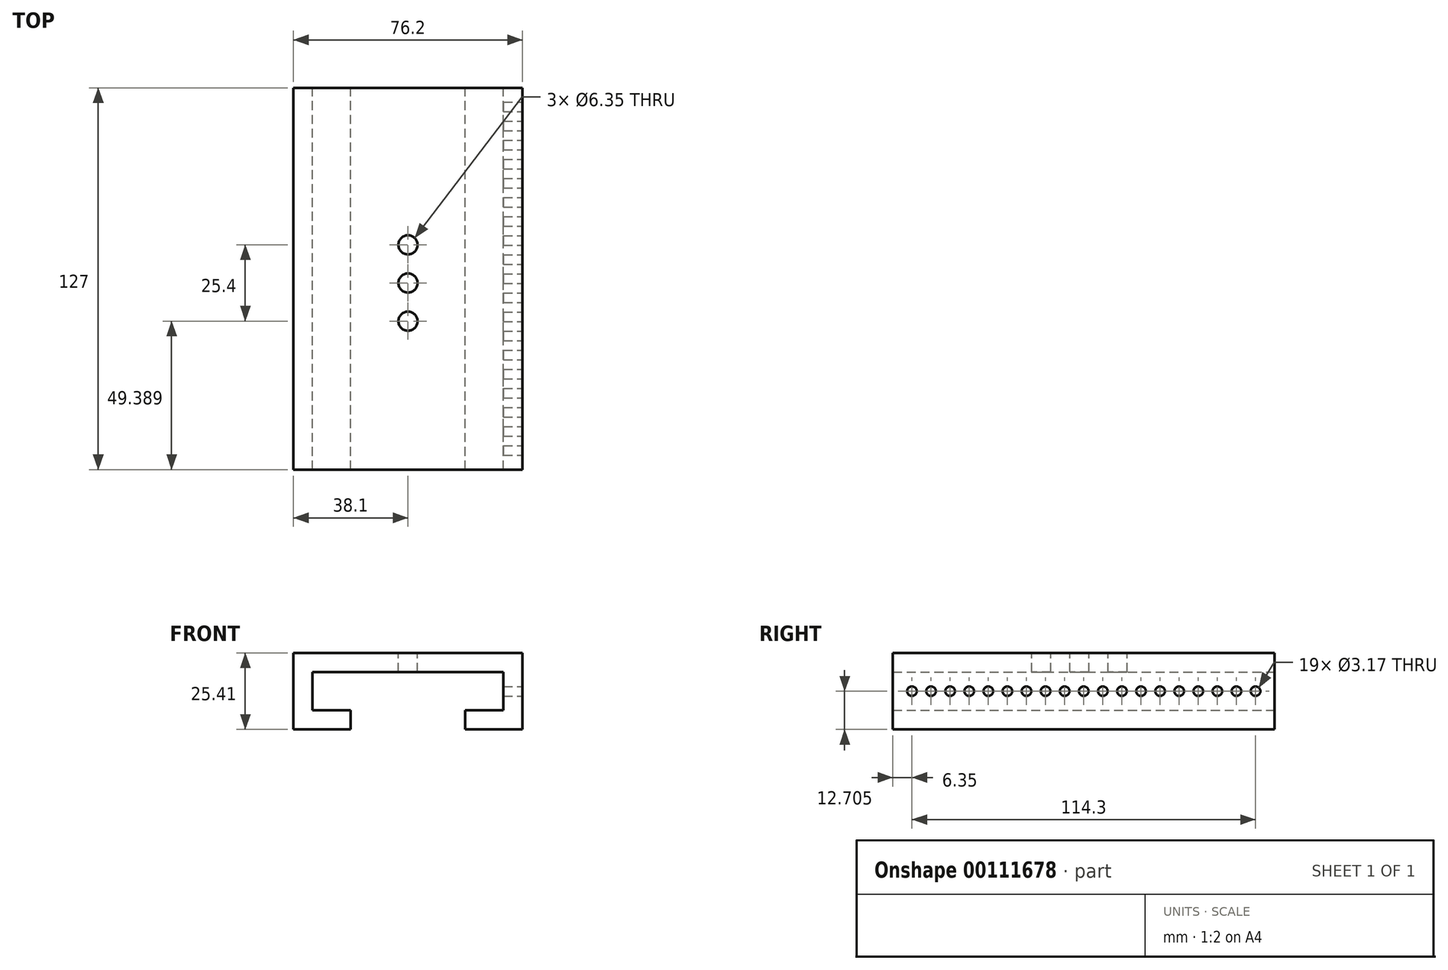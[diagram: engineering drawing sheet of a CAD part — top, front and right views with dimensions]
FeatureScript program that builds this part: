
annotation { "Feature Type Name" : "Feature", "Feature Type Description" : "" }
export const myFeature = defineFeature(function(context is Context, id is Id, definition is map)
    precondition{}
    {
        {
            var Q0;
            Q0=qCreatedBy(makeId("Front.planeOp"),FACE);
            var sketch = newSketch(context, id + "F0", { "sketchPlane" : qUnion([Q0])});
            skLineSegment(sketch, "E0.bottom", {"start": v(31.75, 3.17) * mm, "end": v(-31.75, 3.17) * mm});
            skLineSegment(sketch, "E0.top", {"start": v(31.75, -3.18) * mm, "end": v(-31.75, -3.18) * mm});
            skPoint(sketch, "E0.middle", {"position": v(0, 0) * mm});
            skLineSegment(sketch, "E1.bottom", {"start": v(31.75, 3.17) * mm, "end": v(38.1, 3.17) * mm});
            skLineSegment(sketch, "E2.bottom", {"start": v(-31.75, 3.17) * mm, "end": v(-38.1, 3.17) * mm});
            skLineSegment(sketch, "E3", {"start": v(-31.75, -3.18) * mm, "end": v(-31.75, -15.88) * mm});
            skLineSegment(sketch, "E4", {"start": v(-31.75, -15.88) * mm, "end": v(-19.05, -15.88) * mm});
            skLineSegment(sketch, "E5", {"start": v(-19.05, -15.88) * mm, "end": v(-19.05, -22.23) * mm});
            skLineSegment(sketch, "E6", {"start": v(-19.05, -22.23) * mm, "end": v(-38.1, -22.23) * mm});
            skLineSegment(sketch, "E7", {"start": v(-38.1, -22.23) * mm, "end": v(-38.1, 3.17) * mm});
            skLineSegment(sketch, "E8", {"start": v(31.75, -3.18) * mm, "end": v(31.75, -15.88) * mm});
            skLineSegment(sketch, "E9", {"start": v(31.75, -15.88) * mm, "end": v(19.05, -15.88) * mm});
            skLineSegment(sketch, "E10", {"start": v(19.05, -15.88) * mm, "end": v(19.05, -22.23) * mm});
            skLineSegment(sketch, "E11", {"start": v(19.05, -22.23) * mm, "end": v(38.1, -22.23) * mm});
            skLineSegment(sketch, "E12", {"start": v(38.1, -22.23) * mm, "end": v(38.1, 3.17) * mm});
            skSolve(sketch);
        }
        {
            var Q0;
            Q0=makeQuery(id+"F0.imprint","IMPRINT",FACE,{"disambiguationData":[TD([[makeQuery(id+"F0.imprint","IMPRINT",EDGE,{"derivedFrom":sQuery(id+"F0.wireOp",EDGE,"E0.bottom")}),1.0]])]});
            extrude(context, id + "F1", {"entities" : qUnion([Q0]), "endBound" : BoundingType.SYMMETRIC, "depth" : 127 * mm});
        }
        {
            var Q0;
            {var subQ0=sQuery(id+"F0.wireOp",EDGE,"E2.bottom");var subQ1=sQuery(id+"F0.wireOp",EDGE,"E1.bottom");var subQ2=sQuery(id+"F0.wireOp",EDGE,"E0.bottom");Q0=makeQuery(id+"FXCp8q9W37Aup2r_1.boolean.opBoolean","MERGE",FACE,{"derivedFrom":[makeQuery(id+"F1.opExtrude","SWEPT_FACE",FACE,{"disambiguationData":[OSD([subQ2,subQ1,subQ0])]}),makeQuery(id+"FXCp8q9W37Aup2r_1.opExtrude","SWEPT_FACE",FACE,{"disambiguationData":[OSD([subQ2,subQ1,subQ0])]})]});}
            var sketch = newSketch(context, id + "F2", { "sketchPlane" : qUnion([Q0])});
            skCircle(sketch, "E13", {"center": v(0, -1.41) * mm, "radius": 3.18 * mm});
            skCircle(sketch, "E14", {"center": v(0, 11.29) * mm, "radius": 3.18 * mm});
            skCircle(sketch, "E15", {"center": v(0, -14.11) * mm, "radius": 3.18 * mm});
            skSolve(sketch);
        }
        {
            var Q0;
            {var subQ0=sQuery(id+"F0.wireOp",EDGE,"E12");Q0=makeQuery(id+"FXCp8q9W37Aup2r_1.boolean.opBoolean","MERGE",FACE,{"derivedFrom":[makeQuery(id+"F1.opExtrude","SWEPT_FACE",FACE,{"disambiguationData":[OSD([subQ0])]}),makeQuery(id+"FXCp8q9W37Aup2r_1.opExtrude","SWEPT_FACE",FACE,{"disambiguationData":[OSD([subQ0])]})]});}
            var sketch = newSketch(context, id + "F3", { "sketchPlane" : qUnion([Q0])});
            skCircle(sketch, "E16", {"center": v(-50.8, -9.52) * mm, "radius": 1.59 * mm});
            skCircle(sketch, "E17.1.0.0", {"center": v(-44.45, -9.53) * mm, "radius": 1.59 * mm});
            skCircle(sketch, "E17.2.0.0", {"center": v(-38.1, -9.53) * mm, "radius": 1.59 * mm});
            skCircle(sketch, "E17.3.0.0", {"center": v(-31.75, -9.52) * mm, "radius": 1.59 * mm});
            skCircle(sketch, "E17.4.0.0", {"center": v(-25.4, -9.52) * mm, "radius": 1.59 * mm});
            skCircle(sketch, "E17.5.0.0", {"center": v(-19.05, -9.52) * mm, "radius": 1.59 * mm});
            skCircle(sketch, "E17.6.0.0", {"center": v(-12.7, -9.52) * mm, "radius": 1.59 * mm});
            skCircle(sketch, "E17.7.0.0", {"center": v(-6.35, -9.52) * mm, "radius": 1.59 * mm});
            skCircle(sketch, "E17.8.0.0", {"center": v(0, -9.52) * mm, "radius": 1.59 * mm});
            skCircle(sketch, "E17.9.0.0", {"center": v(6.35, -9.52) * mm, "radius": 1.59 * mm});
            skCircle(sketch, "E18.1.0.0", {"center": v(-57.15, -9.52) * mm, "radius": 1.59 * mm});
            skCircle(sketch, "E19.1.0.0", {"center": v(12.7, -9.52) * mm, "radius": 1.59 * mm});
            skCircle(sketch, "E19.2.0.0", {"center": v(19.05, -9.52) * mm, "radius": 1.59 * mm});
            skCircle(sketch, "E19.3.0.0", {"center": v(25.4, -9.52) * mm, "radius": 1.59 * mm});
            skCircle(sketch, "E19.4.0.0", {"center": v(31.75, -9.52) * mm, "radius": 1.59 * mm});
            skCircle(sketch, "E19.5.0.0", {"center": v(38.1, -9.52) * mm, "radius": 1.59 * mm});
            skCircle(sketch, "E19.6.0.0", {"center": v(44.45, -9.52) * mm, "radius": 1.59 * mm});
            skCircle(sketch, "E19.7.0.0", {"center": v(50.8, -9.52) * mm, "radius": 1.59 * mm});
            skCircle(sketch, "E19.8.0.0", {"center": v(57.15, -9.52) * mm, "radius": 1.59 * mm});
            skLineSegment(sketch, "E19.direction1", {"start": v(6.35, -9.52) * mm, "end": v(12.7, -9.52) * mm, "construction": true});
            skSolve(sketch);
        }
        {
            var Q0;
            Q0=makeQuery(id+"F3.imprint","IMPRINT",FACE,{"disambiguationData":[TD([[makeQuery(id+"F3.imprint","IMPRINT",EDGE,{"derivedFrom":sQuery(id+"F3.wireOp",EDGE,"E18.9.0.0")}),1.0]])]});
            var Q1;
            Q1=makeQuery(id+"F3.imprint","IMPRINT",FACE,{"disambiguationData":[TD([[makeQuery(id+"F3.imprint","IMPRINT",EDGE,{"derivedFrom":sQuery(id+"F3.wireOp",EDGE,"E18.8.0.0")}),1.0]])]});
            var Q2;
            Q2=makeQuery(id+"F3.imprint","IMPRINT",FACE,{"disambiguationData":[TD([[makeQuery(id+"F3.imprint","IMPRINT",EDGE,{"derivedFrom":sQuery(id+"F3.wireOp",EDGE,"E18.7.0.0")}),1.0]])]});
            var Q3;
            Q3=makeQuery(id+"F3.imprint","IMPRINT",FACE,{"disambiguationData":[TD([[makeQuery(id+"F3.imprint","IMPRINT",EDGE,{"derivedFrom":sQuery(id+"F3.wireOp",EDGE,"E18.6.0.0")}),1.0]])]});
            var Q4;
            Q4=makeQuery(id+"F3.imprint","IMPRINT",FACE,{"disambiguationData":[TD([[makeQuery(id+"F3.imprint","IMPRINT",EDGE,{"derivedFrom":sQuery(id+"F3.wireOp",EDGE,"E18.5.0.0")}),1.0]])]});
            var Q5;
            Q5=makeQuery(id+"F3.imprint","IMPRINT",FACE,{"disambiguationData":[TD([[makeQuery(id+"F3.imprint","IMPRINT",EDGE,{"derivedFrom":sQuery(id+"F3.wireOp",EDGE,"E18.4.0.0")}),1.0]])]});
            var Q6;
            Q6=makeQuery(id+"F3.imprint","IMPRINT",FACE,{"disambiguationData":[TD([[makeQuery(id+"F3.imprint","IMPRINT",EDGE,{"derivedFrom":sQuery(id+"F3.wireOp",EDGE,"E18.3.0.0")}),1.0]])]});
            var Q7;
            Q7=makeQuery(id+"F3.imprint","IMPRINT",FACE,{"disambiguationData":[TD([[makeQuery(id+"F3.imprint","IMPRINT",EDGE,{"derivedFrom":sQuery(id+"F3.wireOp",EDGE,"E18.2.0.0")}),1.0]])]});
            var Q8;
            Q8=makeQuery(id+"F3.imprint","IMPRINT",FACE,{"disambiguationData":[TD([[makeQuery(id+"F3.imprint","IMPRINT",EDGE,{"derivedFrom":sQuery(id+"F3.wireOp",EDGE,"E18.1.0.0")}),1.0]])]});
            var Q9;
            Q9=makeQuery(id+"F3.imprint","IMPRINT",FACE,{"disambiguationData":[TD([[makeQuery(id+"F3.imprint","IMPRINT",EDGE,{"derivedFrom":sQuery(id+"F3.wireOp",EDGE,"E16")}),1.0]])]});
            var Q10;
            Q10=makeQuery(id+"F3.imprint","IMPRINT",FACE,{"disambiguationData":[TD([[makeQuery(id+"F3.imprint","IMPRINT",EDGE,{"derivedFrom":sQuery(id+"F3.wireOp",EDGE,"E17.1.0.0")}),1.0]])]});
            var Q11;
            Q11=makeQuery(id+"F3.imprint","IMPRINT",FACE,{"disambiguationData":[TD([[makeQuery(id+"F3.imprint","IMPRINT",EDGE,{"derivedFrom":sQuery(id+"F3.wireOp",EDGE,"E17.2.0.0")}),1.0]])]});
            var Q12;
            Q12=makeQuery(id+"F3.imprint","IMPRINT",FACE,{"disambiguationData":[TD([[makeQuery(id+"F3.imprint","IMPRINT",EDGE,{"derivedFrom":sQuery(id+"F3.wireOp",EDGE,"E17.3.0.0")}),1.0]])]});
            var Q13;
            Q13=makeQuery(id+"F3.imprint","IMPRINT",FACE,{"disambiguationData":[TD([[makeQuery(id+"F3.imprint","IMPRINT",EDGE,{"derivedFrom":sQuery(id+"F3.wireOp",EDGE,"E17.4.0.0")}),1.0]])]});
            var Q14;
            Q14=makeQuery(id+"F3.imprint","IMPRINT",FACE,{"disambiguationData":[TD([[makeQuery(id+"F3.imprint","IMPRINT",EDGE,{"derivedFrom":sQuery(id+"F3.wireOp",EDGE,"E17.5.0.0")}),1.0]])]});
            var Q15;
            Q15=makeQuery(id+"F3.imprint","IMPRINT",FACE,{"disambiguationData":[TD([[makeQuery(id+"F3.imprint","IMPRINT",EDGE,{"derivedFrom":sQuery(id+"F3.wireOp",EDGE,"E17.6.0.0")}),1.0]])]});
            var Q16;
            Q16=makeQuery(id+"F3.imprint","IMPRINT",FACE,{"disambiguationData":[TD([[makeQuery(id+"F3.imprint","IMPRINT",EDGE,{"derivedFrom":sQuery(id+"F3.wireOp",EDGE,"E17.7.0.0")}),1.0]])]});
            var Q17;
            Q17=makeQuery(id+"F3.imprint","IMPRINT",FACE,{"disambiguationData":[TD([[makeQuery(id+"F3.imprint","IMPRINT",EDGE,{"derivedFrom":sQuery(id+"F3.wireOp",EDGE,"E17.8.0.0")}),1.0]])]});
            var Q18;
            Q18=makeQuery(id+"F3.imprint","IMPRINT",FACE,{"disambiguationData":[TD([[makeQuery(id+"F3.imprint","IMPRINT",EDGE,{"derivedFrom":sQuery(id+"F3.wireOp",EDGE,"E17.9.0.0")}),1.0]])]});
            extrude(context, id + "F4", {"entities" : qUnion([Q0, Q1, Q2, Q3, Q4, Q5, Q6, Q7, Q8, Q9, Q10, Q11, Q12, Q13, Q14, Q15, Q16, Q17, Q18]), "operationType" : NewBodyOperationType.REMOVE, "oppositeDirection" : true, "depth" : 6.35 * mm});
        }
        {
            var Q0;
            Q0=makeQuery(id+"F2.imprint","IMPRINT",FACE,{"disambiguationData":[TD([[makeQuery(id+"F2.imprint","IMPRINT",EDGE,{"derivedFrom":sQuery(id+"F2.wireOp",EDGE,"E14")}),1.0]])]});
            var Q1;
            Q1=makeQuery(id+"F2.imprint","IMPRINT",FACE,{"disambiguationData":[TD([[makeQuery(id+"F2.imprint","IMPRINT",EDGE,{"derivedFrom":sQuery(id+"F2.wireOp",EDGE,"E13")}),1.0]])]});
            var Q2;
            Q2=makeQuery(id+"F2.imprint","IMPRINT",FACE,{"disambiguationData":[TD([[makeQuery(id+"F2.imprint","IMPRINT",EDGE,{"derivedFrom":sQuery(id+"F2.wireOp",EDGE,"E15")}),1.0]])]});
            extrude(context, id + "F5", {"entities" : qUnion([Q0, Q1, Q2]), "operationType" : NewBodyOperationType.REMOVE, "oppositeDirection" : true, "depth" : 6.35 * mm});
        }
        {
            var Q0;
            Q0=makeQuery(id+"F3.imprint","IMPRINT",FACE,{"disambiguationData":[TD([[makeQuery(id+"F3.imprint","IMPRINT",EDGE,{"derivedFrom":sQuery(id+"F3.wireOp",EDGE,"E19.1.0.0")}),1.0]])]});
            var Q1;
            Q1=makeQuery(id+"F3.imprint","IMPRINT",FACE,{"disambiguationData":[TD([[makeQuery(id+"F3.imprint","IMPRINT",EDGE,{"derivedFrom":sQuery(id+"F3.wireOp",EDGE,"E19.2.0.0")}),1.0]])]});
            var Q2;
            Q2=makeQuery(id+"F3.imprint","IMPRINT",FACE,{"disambiguationData":[TD([[makeQuery(id+"F3.imprint","IMPRINT",EDGE,{"derivedFrom":sQuery(id+"F3.wireOp",EDGE,"E19.3.0.0")}),1.0]])]});
            var Q3;
            Q3=makeQuery(id+"F3.imprint","IMPRINT",FACE,{"disambiguationData":[TD([[makeQuery(id+"F3.imprint","IMPRINT",EDGE,{"derivedFrom":sQuery(id+"F3.wireOp",EDGE,"E19.4.0.0")}),1.0]])]});
            var Q4;
            Q4=makeQuery(id+"F3.imprint","IMPRINT",FACE,{"disambiguationData":[TD([[makeQuery(id+"F3.imprint","IMPRINT",EDGE,{"derivedFrom":sQuery(id+"F3.wireOp",EDGE,"E19.5.0.0")}),1.0]])]});
            var Q5;
            Q5=makeQuery(id+"F3.imprint","IMPRINT",FACE,{"disambiguationData":[TD([[makeQuery(id+"F3.imprint","IMPRINT",EDGE,{"derivedFrom":sQuery(id+"F3.wireOp",EDGE,"E19.6.0.0")}),1.0]])]});
            var Q6;
            Q6=makeQuery(id+"F3.imprint","IMPRINT",FACE,{"disambiguationData":[TD([[makeQuery(id+"F3.imprint","IMPRINT",EDGE,{"derivedFrom":sQuery(id+"F3.wireOp",EDGE,"E19.7.0.0")}),1.0]])]});
            var Q7;
            Q7=makeQuery(id+"F3.imprint","IMPRINT",FACE,{"disambiguationData":[TD([[makeQuery(id+"F3.imprint","IMPRINT",EDGE,{"derivedFrom":sQuery(id+"F3.wireOp",EDGE,"E19.8.0.0")}),1.0]])]});
            extrude(context, id + "F6", {"entities" : qUnion([Q0, Q1, Q2, Q3, Q4, Q5, Q6, Q7]), "operationType" : NewBodyOperationType.REMOVE, "oppositeDirection" : true, "depth" : 6.35 * mm});
        }
    });
